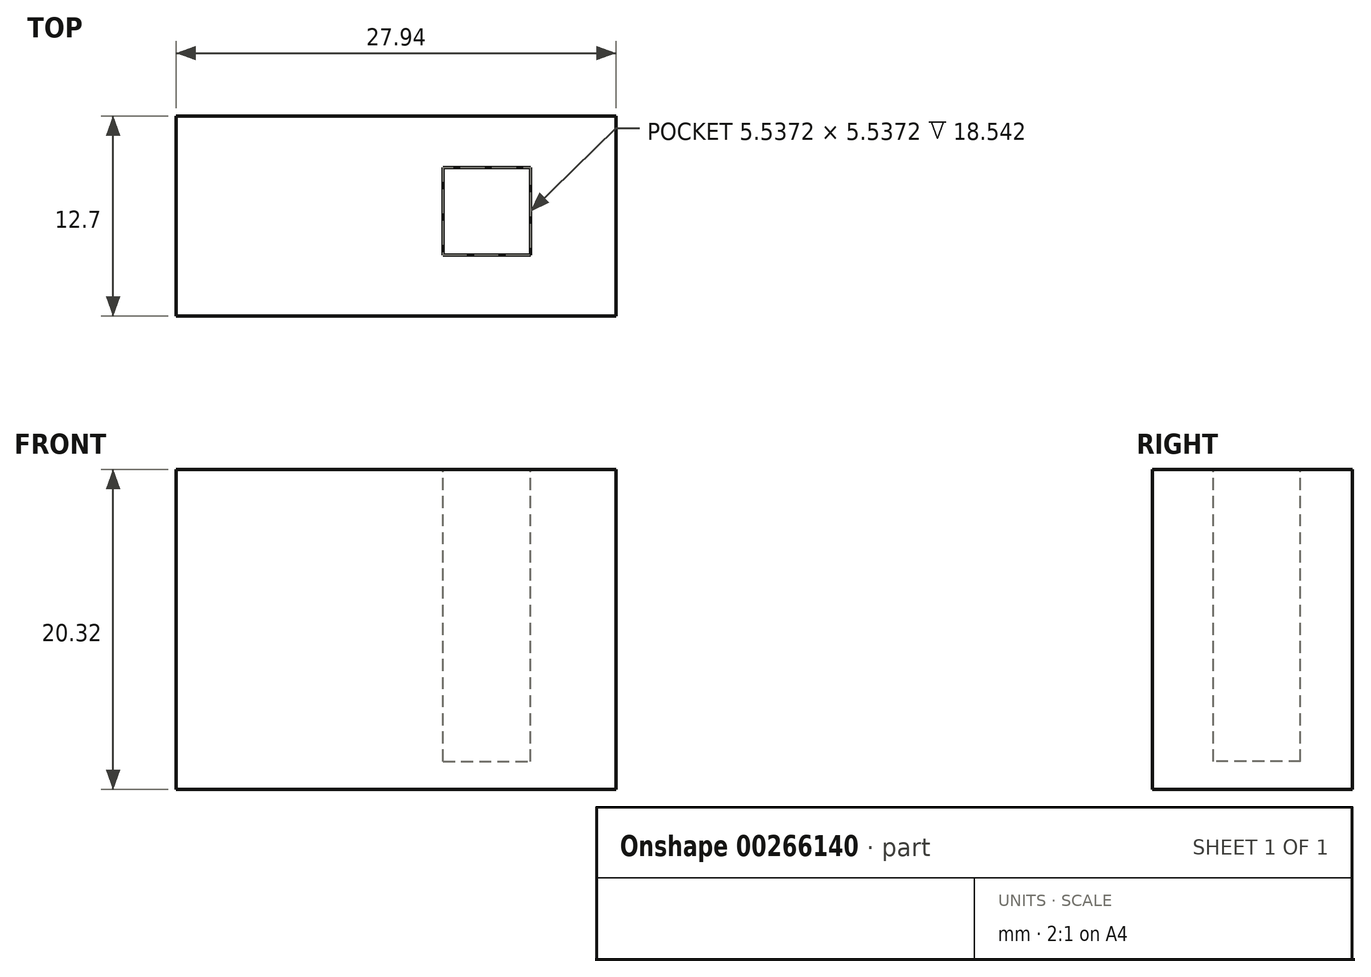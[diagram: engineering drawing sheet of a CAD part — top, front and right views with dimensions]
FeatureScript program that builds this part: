
annotation { "Feature Type Name" : "Feature", "Feature Type Description" : "" }
export const myFeature = defineFeature(function(context is Context, id is Id, definition is map)
    precondition{}
    {
        {
            var Q0;
            Q0=qCreatedBy(makeId("Front.planeOp"),FACE);
            var sketch = newSketch(context, id + "F0", { "sketchPlane" : qUnion([Q0])});
            skLineSegment(sketch, "E0.bottom", {"start": v(13.97, 10.16) * mm, "end": v(-13.97, 10.16) * mm});
            skLineSegment(sketch, "E0.top", {"start": v(13.97, -10.16) * mm, "end": v(-13.97, -10.16) * mm});
            skLineSegment(sketch, "E0.left", {"start": v(13.97, 10.16) * mm, "end": v(13.97, -10.16) * mm});
            skLineSegment(sketch, "E0.right", {"start": v(-13.97, 10.16) * mm, "end": v(-13.97, -10.16) * mm});
            skPoint(sketch, "E0.middle", {"position": v(0, 0) * mm});
            skSolve(sketch);
        }
        {
            var Q0;
            {var subQ4=sQuery(id+"F0.wireOp",EDGE,"HMXBIAzO-FHkh-AqYh-ONwg-7I9FQ5fUV9Sl");Q0=makeQuery(id+"F0.imprint","IMPRINT",FACE,{"disambiguationData":[TD([[makeQuery(id+"F0.imprint","IMPRINT",EDGE,{"derivedFrom":subQ4}),1.0]])]});}
            var Q1;
            {var subQ0=sQuery(id+"F0.wireOp",EDGE,"tzh9WF8R-HAHd-LTBO-3hLl-sT77aeeRFytH");Q1=makeQuery(id+"F0.imprint","IMPRINT",FACE,{"disambiguationData":[TD([[makeQuery(id+"F0.imprint","IMPRINT",EDGE,{"derivedFrom":subQ0}),-1.0]])]});}
            var Q2;
            Q2=makeQuery(id+"F0.imprint","IMPRINT",FACE,{"disambiguationData":[TD([[makeQuery(id+"F0.imprint","IMPRINT",EDGE,{"derivedFrom":sQuery(id+"F0.wireOp",EDGE,"E0.top")}),-1.0]])]});
            extrude(context, id + "F1", {"entities" : qUnion([Q0, Q1, Q2]), "depth" : 12.7 * mm});
        }
        {
            var Q0;
            Q0=makeQuery(id+"F1.opExtrude","SWEPT_FACE",FACE,{"disambiguationData":[OSD([sQuery(id+"F0.wireOp",EDGE,"E0.bottom")])]});
            var sketch = newSketch(context, id + "F2", { "sketchPlane" : qUnion([Q0])});
            skLineSegment(sketch, "E1.bottom", {"start": v(3, -3.28) * mm, "end": v(8.53, -3.28) * mm});
            skLineSegment(sketch, "E1.top", {"start": v(3, -8.82) * mm, "end": v(8.53, -8.82) * mm});
            skLineSegment(sketch, "E1.left", {"start": v(3, -3.28) * mm, "end": v(3, -8.82) * mm});
            skLineSegment(sketch, "E1.right", {"start": v(8.53, -3.28) * mm, "end": v(8.53, -8.82) * mm});
            skSolve(sketch);
        }
        {
            var Q0;
            Q0 = qSketchRegion(id + "F2", true);
            extrude(context, id + "F3", {"entities" : qUnion([Q0]), "operationType" : NewBodyOperationType.REMOVE, "oppositeDirection" : true, "depth" : 18.54 * mm});
        }
    });
